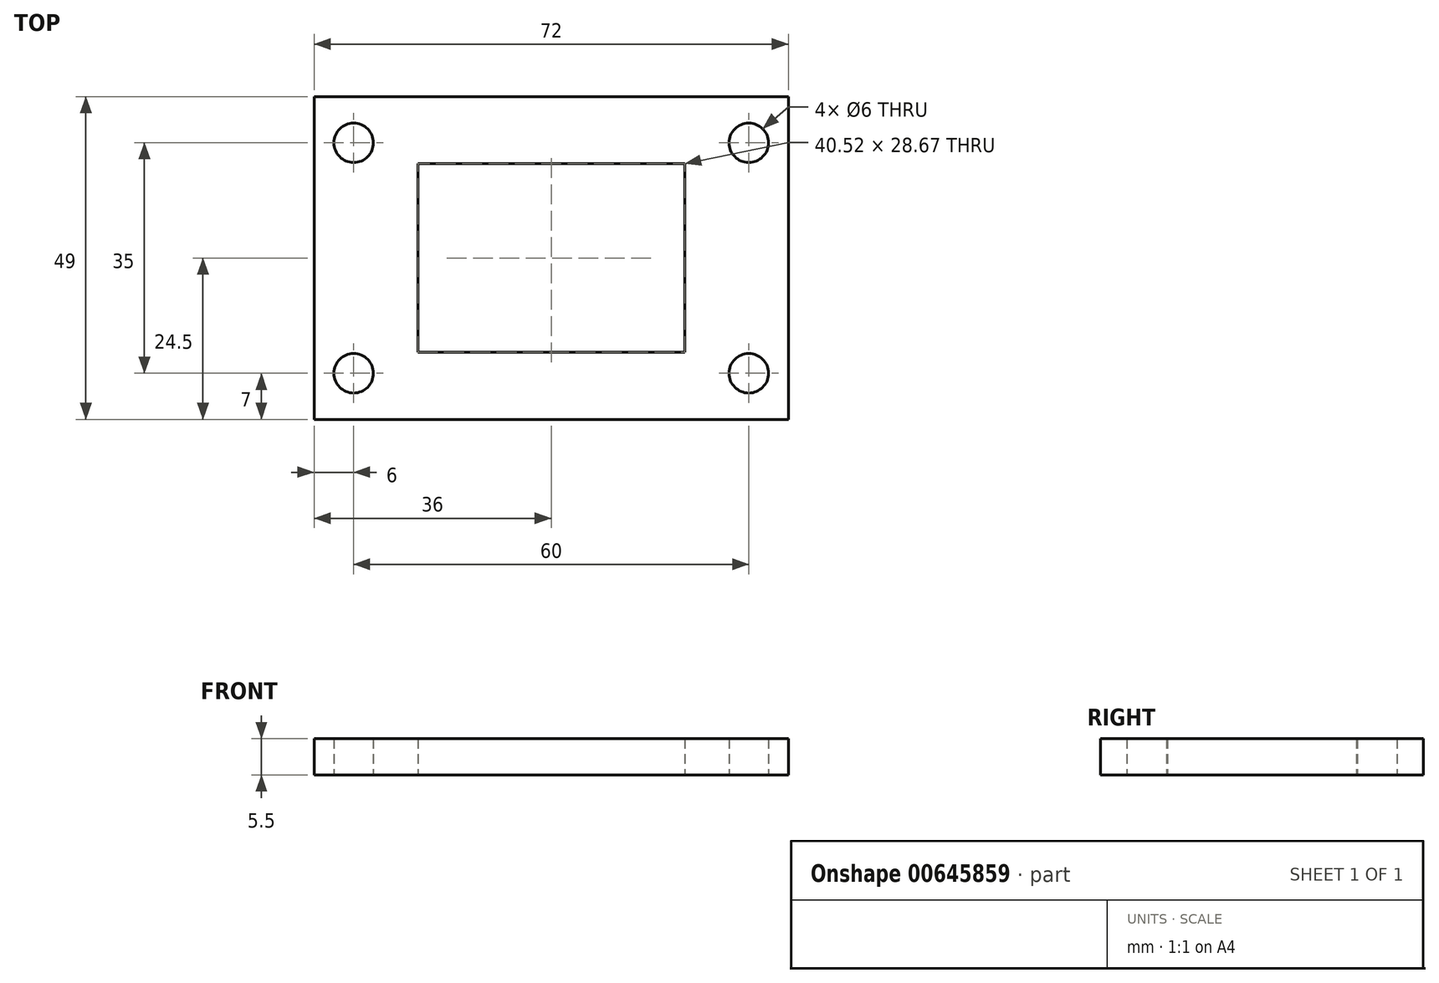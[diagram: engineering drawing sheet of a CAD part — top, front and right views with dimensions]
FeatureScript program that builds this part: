
annotation { "Feature Type Name" : "Feature", "Feature Type Description" : "" }
export const myFeature = defineFeature(function(context is Context, id is Id, definition is map)
    precondition{}
    {
        {
            var Q0;
            Q0=qCreatedBy(makeId("Top.planeOp"),FACE);
            var sketch = newSketch(context, id + "F0", { "sketchPlane" : qUnion([Q0])});
            skLineSegment(sketch, "E0.bottom", {"start": v(36, -24.5) * mm, "end": v(-36, -24.5) * mm});
            skLineSegment(sketch, "E0.top", {"start": v(36, 24.5) * mm, "end": v(-36, 24.5) * mm});
            skLineSegment(sketch, "E0.left", {"start": v(36, -24.5) * mm, "end": v(36, 24.5) * mm});
            skLineSegment(sketch, "E0.right", {"start": v(-36, -24.5) * mm, "end": v(-36, 24.5) * mm});
            skPoint(sketch, "E0.middle", {"position": v(0, 0) * mm});
            skLineSegment(sketch, "E1.bottom", {"start": v(30, -17.5) * mm, "end": v(-30, -17.5) * mm});
            skLineSegment(sketch, "E1.top", {"start": v(30, 17.5) * mm, "end": v(-30, 17.5) * mm});
            skLineSegment(sketch, "E1.left", {"start": v(30, -17.5) * mm, "end": v(30, 17.5) * mm});
            skLineSegment(sketch, "E1.right", {"start": v(-30, -17.5) * mm, "end": v(-30, 17.5) * mm});
            skCircle(sketch, "E2", {"center": v(-30, 17.5) * mm, "radius": 3 * mm});
            skCircle(sketch, "E3", {"center": v(30, 17.5) * mm, "radius": 3 * mm});
            skCircle(sketch, "E4", {"center": v(-30, -17.5) * mm, "radius": 3 * mm});
            skCircle(sketch, "E5", {"center": v(30, -17.5) * mm, "radius": 3 * mm});
            skSolve(sketch);
        }
        {
            var Q0;
            Q0=makeQuery(id+"F0.imprint","IMPRINT",FACE,{"disambiguationData":[TD([[makeQuery(id+"F0.imprint","IMPRINT",EDGE,{"derivedFrom":sQuery(id+"F0.wireOp",EDGE,"E0.bottom")}),-1.0]])]});
            var Q1;
            {var subQ5=sQuery(id+"F0.wireOp",EDGE,"E5");var subQ10=sQuery(id+"F0.wireOp",EDGE,"E1.bottom");var subQ11=makeQuery(id+"F0.imprint","INTERSECT",VERTEX,{"derivedFrom":[subQ10,subQ5]});Q1=makeQuery(id+"F0.imprint","IMPRINT",FACE,{"disambiguationData":[TD([[makeQuery(id+"F0.imprint","IMPRINT",EDGE,{"disambiguationData":[TD([[subQ11,-1.0]])],"derivedFrom":subQ10}),-1.0]])]});}
            extrude(context, id + "F1", {"entities" : qUnion([Q0, Q1]), "endBound" : BoundingType.SYMMETRIC, "depth" : 5.5 * mm, "offsetDistance" : 25 * mm});
        }
        {
            var Q0;
            Q0=makeQuery(id+"F1.opExtrude","CAP_FACE",FACE,{"disambiguationData":[OSD([sQuery(id+"F0.wireOp",EDGE,"E0.bottom"),sQuery(id+"F0.wireOp",EDGE,"E0.top"),sQuery(id+"F0.wireOp",EDGE,"E0.left"),sQuery(id+"F0.wireOp",EDGE,"E0.right"),sQuery(id+"F0.wireOp",EDGE,"E2"),sQuery(id+"F0.wireOp",EDGE,"E3"),sQuery(id+"F0.wireOp",EDGE,"E4"),sQuery(id+"F0.wireOp",EDGE,"E5")])],"isStart":true});
            var sketch = newSketch(context, id + "F2", { "sketchPlane" : qUnion([Q0])});
            skLineSegment(sketch, "E6.bottom", {"start": v(20.26, 14.33) * mm, "end": v(-20.26, 14.33) * mm});
            skLineSegment(sketch, "E6.top", {"start": v(20.26, -14.33) * mm, "end": v(-20.26, -14.33) * mm});
            skLineSegment(sketch, "E6.left", {"start": v(20.26, 14.33) * mm, "end": v(20.26, -14.33) * mm});
            skLineSegment(sketch, "E6.right", {"start": v(-20.26, 14.33) * mm, "end": v(-20.26, -14.33) * mm});
            skPoint(sketch, "E6.middle", {"position": v(0, 0) * mm});
            skSolve(sketch);
        }
        {
            var Q0;
            Q0=makeQuery(id+"F2.imprint","IMPRINT",FACE,{"disambiguationData":[TD([[makeQuery(id+"F2.imprint","IMPRINT",EDGE,{"derivedFrom":sQuery(id+"F2.wireOp",EDGE,"E6.bottom")}),1.0]])]});
            extrude(context, id + "F3", {"entities" : qUnion([Q0]), "operationType" : NewBodyOperationType.REMOVE, "oppositeDirection" : true, "depth" : 25 * mm, "offsetDistance" : 25 * mm});
        }
    });
